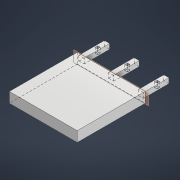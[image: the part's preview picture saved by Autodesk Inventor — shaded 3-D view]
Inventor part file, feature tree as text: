
AUTODESK INVENTOR PART (.ipt)
format: ipt  version: 2022 (Build 260153000, 153)  size: 148,992 bytes
history: native  units: in
note: dims shown in document units (in); Inventor stores cm internally (conversion verified against a paired STEP export)
features: reference x16, extrude x4, sketch x4, other x4, plane x2, fillet x1
ambient origin geometry x8: Origin, YZ Plane, XZ Plane, XY Plane, X Axis, Y Axis, Z Axis, Center Point
bodies: Solid1 (feature_tree)
feature tree (31):
  plane  "Work Plane1"
  extrude  "Extrusion1"  Depth=0.15in TaperAngle=0.0deg
  extrude  "Extrusion2"  Depth=2.0in
  plane  "Work Plane2"
  extrude  "Extrusion3"  Depth=0.5363in
  extrude  "Extrusion4"  Depth=0.125in
  fillet  "Fillet1"  Radius=0.0344in
  sketch  "Sketch1"  dims[d0=0.75in d1=0.0in d2=0.15in d3=0.0in]
  reference  "Reference1"
  sketch  "Sketch2"  dims[d4=2.0in d5=0.0in d6=0.626in]
  reference  "Reference2"
  reference  "Reference3"
  reference  "Reference4"
  reference  "Reference5"
  reference  "Reference6"
  reference  "Reference7"
  reference  "Reference8"
  reference  "Reference9"
  reference  "Reference10"
  reference  "Reference11"
  reference  "Reference12"
  reference  "Reference13"
  sketch  "Sketch3"  dims[d7=0.626in d8=0.5363in]
  reference  "Reference14"
  sketch  "Sketch4"  dims[d9=0.3in d10=0.0in d11=0.125in d12=0.0344in]
  reference  "Reference15"
  reference  "Reference16"
  parser-record x1  (decoder bookkeeping rows leaked as tree rows — omitted from the tree; the rows remain in map.json)
  other  "Prototype Assembly.iam"
  other  "Vertical Beam Prototype:1"
  other  "hc-sr04:1"
note: 1 file-system path scrubbed to <path> (originals preserved in map.json)
